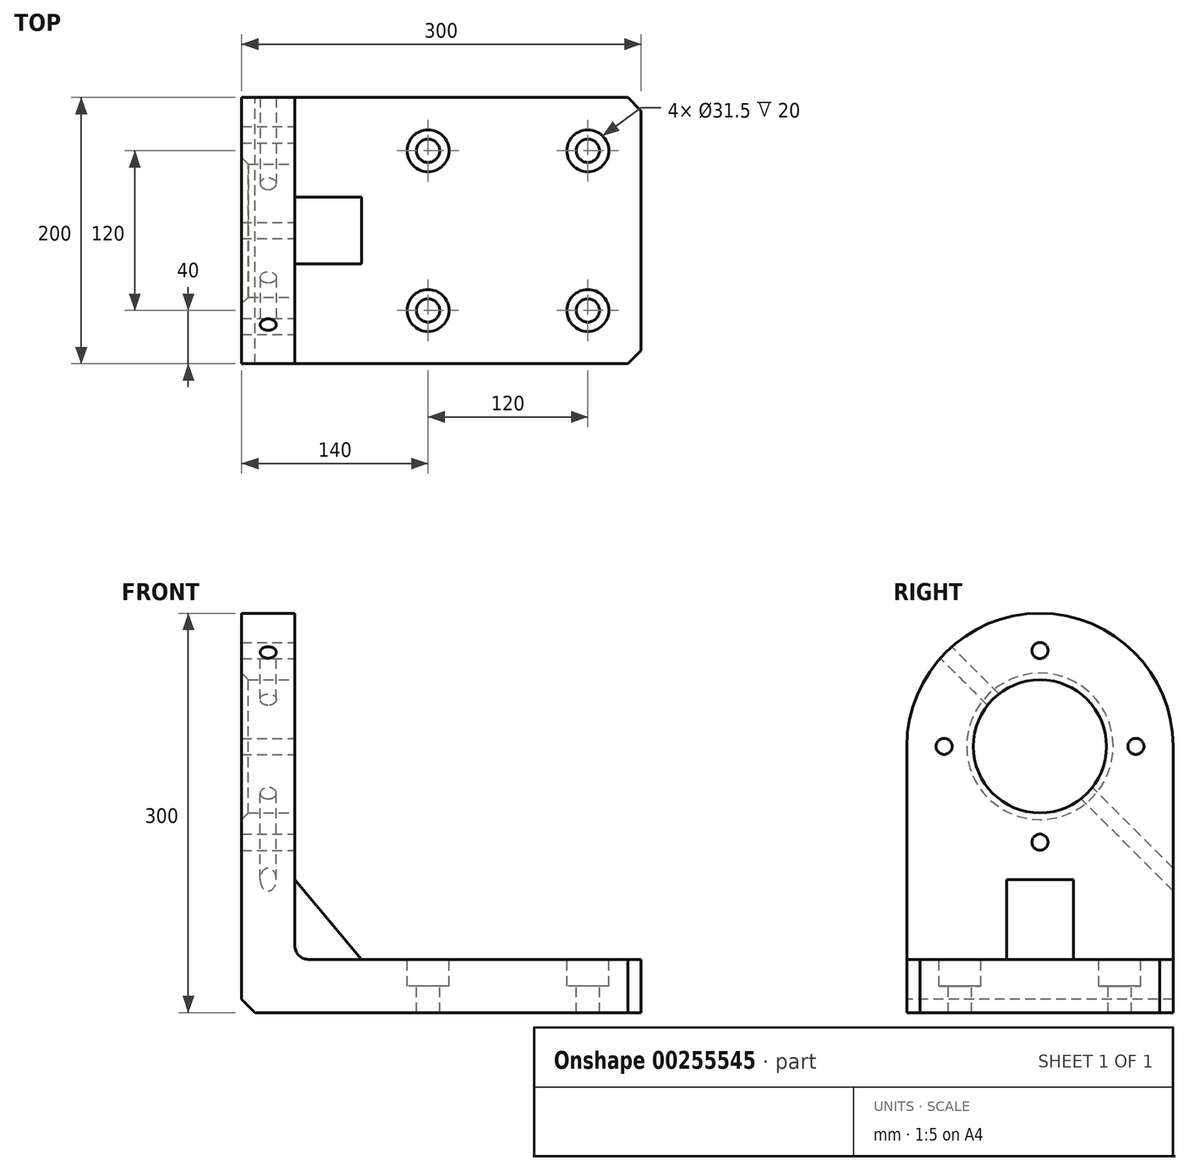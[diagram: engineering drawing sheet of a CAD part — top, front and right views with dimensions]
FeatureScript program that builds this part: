
annotation { "Feature Type Name" : "Feature", "Feature Type Description" : "" }
export const myFeature = defineFeature(function(context is Context, id is Id, definition is map)
    precondition{}
    {
        {
            var Q0;
            Q0=qCreatedBy(makeId("Front.planeOp"),FACE);
            var sketch = newSketch(context, id + "F0", { "sketchPlane" : qUnion([Q0])});
            skLineSegment(sketch, "E0", {"start": v(0, 0) * mm, "end": v(-300, 0) * mm});
            skLineSegment(sketch, "E1", {"start": v(-300, 0) * mm, "end": v(-300, 300) * mm});
            skLineSegment(sketch, "E2", {"start": v(0, 0) * mm, "end": v(0, 40) * mm});
            skLineSegment(sketch, "E3", {"start": v(-300, 300) * mm, "end": v(-260, 300) * mm});
            skLineSegment(sketch, "E4", {"start": v(0, 40) * mm, "end": v(-260, 40) * mm});
            skLineSegment(sketch, "E5", {"start": v(-260, 300) * mm, "end": v(-260, 40) * mm});
            skSolve(sketch);
        }
        {
            var Q0;
            Q0 = qSketchRegion(id + "F0", true);
            extrude(context, id + "F1", {"entities" : qUnion([Q0]), "oppositeDirection" : true, "depth" : 200 * mm});
        }
        {
            var Q0;
            Q0=makeQuery(id+"F1.opExtrude","SWEPT_FACE",FACE,{"disambiguationData":[OSD([sQuery(id+"F0.wireOp",EDGE,"E4")])]});
            var sketch = newSketch(context, id + "F2", { "sketchPlane" : qUnion([Q0])});
            skLineSegment(sketch, "E6", {"start": v(0, 160) * mm, "end": v(-40, 160) * mm, "construction": true});
            skLineSegment(sketch, "E7", {"start": v(0, 40) * mm, "end": v(-40, 40) * mm, "construction": true});
            skLineSegment(sketch, "E8", {"start": v(-40, 160) * mm, "end": v(-40, 40) * mm});
            skCircle(sketch, "E9", {"center": v(-40, 160) * mm, "radius": 15.75 * mm});
            skCircle(sketch, "E10", {"center": v(-40, 40) * mm, "radius": 15.75 * mm});
            skCircle(sketch, "E11", {"center": v(-160, 160) * mm, "radius": 15.75 * mm});
            skCircle(sketch, "E12", {"center": v(-160, 40) * mm, "radius": 15.75 * mm});
            skCircle(sketch, "E13", {"center": v(-160, 160) * mm, "radius": 8.75 * mm});
            skCircle(sketch, "E14", {"center": v(-160, 40) * mm, "radius": 8.75 * mm});
            skCircle(sketch, "E15", {"center": v(-40, 40) * mm, "radius": 8.75 * mm});
            skCircle(sketch, "E16", {"center": v(-40, 160) * mm, "radius": 8.75 * mm});
            skSolve(sketch);
        }
        {
            var Q0;
            Q0=makeQuery(id+"F2.imprint","IMPRINT",FACE,{"disambiguationData":[TD([[makeQuery(id+"F2.imprint","IMPRINT",EDGE,{"derivedFrom":sQuery(id+"F2.wireOp",EDGE,"E11")}),1.0]])]});
            var Q1;
            Q1=makeQuery(id+"F2.imprint","IMPRINT",FACE,{"disambiguationData":[TD([[makeQuery(id+"F2.imprint","IMPRINT",EDGE,{"derivedFrom":sQuery(id+"F2.wireOp",EDGE,"E12")}),1.0]])]});
            var Q2;
            Q2=makeQuery(id+"F2.imprint","IMPRINT",FACE,{"disambiguationData":[TD([[makeQuery(id+"F2.imprint","IMPRINT",EDGE,{"derivedFrom":sQuery(id+"F2.wireOp",EDGE,"E10")}),1.0]])]});
            var Q3;
            Q3=makeQuery(id+"F2.imprint","IMPRINT",FACE,{"disambiguationData":[TD([[makeQuery(id+"F2.imprint","IMPRINT",EDGE,{"derivedFrom":sQuery(id+"F2.wireOp",EDGE,"E9")}),1.0]])]});
            extrude(context, id + "F3", {"entities" : qUnion([Q0, Q1, Q2, Q3]), "operationType" : NewBodyOperationType.REMOVE, "oppositeDirection" : true, "depth" : 20 * mm});
        }
        {
            var Q0;
            Q0=makeQuery(id+"F3.boolean.opBoolean","SPLIT",FACE,{"disambiguationData":[TD([makeQuery(id+"F3.opExtrude","SWEPT_FACE",FACE,{"disambiguationData":[OSD([sQuery(id+"F2.wireOp",EDGE,"E13")])]})])],"derivedFrom":makeQuery(id+"F1.opExtrude","SWEPT_FACE",FACE,{"disambiguationData":[OSD([sQuery(id+"F0.wireOp",EDGE,"E4")])]})});
            var Q1;
            Q1=makeQuery(id+"F3.boolean.opBoolean","SPLIT",FACE,{"disambiguationData":[TD([makeQuery(id+"F3.opExtrude","SWEPT_FACE",FACE,{"disambiguationData":[OSD([sQuery(id+"F2.wireOp",EDGE,"E16")])]})])],"derivedFrom":makeQuery(id+"F1.opExtrude","SWEPT_FACE",FACE,{"disambiguationData":[OSD([sQuery(id+"F0.wireOp",EDGE,"E4")])]})});
            var Q2;
            Q2=makeQuery(id+"F3.boolean.opBoolean","SPLIT",FACE,{"disambiguationData":[TD([makeQuery(id+"F3.opExtrude","SWEPT_FACE",FACE,{"disambiguationData":[OSD([sQuery(id+"F2.wireOp",EDGE,"E15")])]})])],"derivedFrom":makeQuery(id+"F1.opExtrude","SWEPT_FACE",FACE,{"disambiguationData":[OSD([sQuery(id+"F0.wireOp",EDGE,"E4")])]})});
            var Q3;
            Q3=makeQuery(id+"F3.boolean.opBoolean","SPLIT",FACE,{"disambiguationData":[TD([makeQuery(id+"F3.opExtrude","SWEPT_FACE",FACE,{"disambiguationData":[OSD([sQuery(id+"F2.wireOp",EDGE,"E14")])]})])],"derivedFrom":makeQuery(id+"F1.opExtrude","SWEPT_FACE",FACE,{"disambiguationData":[OSD([sQuery(id+"F0.wireOp",EDGE,"E4")])]})});
            extrude(context, id + "F4", {"entities" : qUnion([Q0, Q1, Q2, Q3]), "operationType" : NewBodyOperationType.REMOVE, "endBound" : BoundingType.THROUGH_ALL, "oppositeDirection" : true, "depth" : 25 * mm});
        }
        {
            var Q0;
            Q0=makeQuery(id+"F1.opExtrude","SWEPT_FACE",FACE,{"disambiguationData":[OSD([sQuery(id+"F0.wireOp",EDGE,"E5")])]});
            var sketch = newSketch(context, id + "F5", { "sketchPlane" : qUnion([Q0])});
            skArc(sketch, "E17", {"start": v(200, 200) * mm, "mid": v(100, 300) * mm, "end": v(0, 200) * mm});
            skPoint(sketch, "E18.start.orphan", {"position": v(100, 300) * mm});
            skPoint(sketch, "E19.orphan", {"position": v(200, 200) * mm});
            skCircle(sketch, "E20", {"center": v(100, 200) * mm, "radius": 72 * mm});
            skCircle(sketch, "E21", {"center": v(100, 200) * mm, "radius": 50 * mm});
            skCircle(sketch, "E22", {"center": v(100, 272) * mm, "radius": 5.8 * mm});
            skCircle(sketch, "E23", {"center": v(100, 128) * mm, "radius": 5.8 * mm});
            skCircle(sketch, "E24", {"center": v(172, 200) * mm, "radius": 5.8 * mm});
            skCircle(sketch, "E25", {"center": v(28, 200) * mm, "radius": 5.8 * mm});
            skSolve(sketch);
        }
        {
            var Q0;
            {var subQ0=sQuery(id+"F5.wireOp",EDGE,"E17");var subQ1=sQuery(id+"F0.wireOp",EDGE,"E5");var subQ2=makeQuery(id+"F1.opExtrude","CAP_EDGE",EDGE,{"disambiguationData":[OSD([subQ1])],"isStart":true});var subQ3=makeQuery(id+"F5.imprint","INTERSECT",VERTEX,{"derivedFrom":[subQ2,subQ0]});Q0=makeQuery(id+"F5.imprint","IMPRINT",FACE,{"disambiguationData":[TD([[makeQuery(id+"F5.imprint","IMPRINT",EDGE,{"disambiguationData":[TD([[subQ3,1.0]])],"derivedFrom":subQ0}),-1.0]])]});}
            var Q1;
            {var subQ0=sQuery(id+"F5.wireOp",EDGE,"E17");var subQ1=sQuery(id+"F0.wireOp",EDGE,"E5");var subQ2=makeQuery(id+"F1.opExtrude","CAP_EDGE",EDGE,{"disambiguationData":[OSD([subQ1])],"isStart":false});var subQ3=makeQuery(id+"F5.imprint","INTERSECT",VERTEX,{"derivedFrom":[subQ2,subQ0]});Q1=makeQuery(id+"F5.imprint","IMPRINT",FACE,{"disambiguationData":[TD([[makeQuery(id+"F5.imprint","IMPRINT",EDGE,{"disambiguationData":[TD([[subQ3,-1.0]])],"derivedFrom":subQ0}),-1.0]])]});}
            extrude(context, id + "F6", {"entities" : qUnion([Q0, Q1]), "operationType" : NewBodyOperationType.REMOVE, "oppositeDirection" : true, "depth" : 89 * mm});
        }
        {
            var Q0;
            Q0=makeQuery(id+"F5.imprint","IMPRINT",FACE,{"disambiguationData":[TD([[makeQuery(id+"F5.imprint","IMPRINT",EDGE,{"derivedFrom":sQuery(id+"F5.wireOp",EDGE,"E21")}),1.0]])]});
            extrude(context, id + "F7", {"entities" : qUnion([Q0]), "operationType" : NewBodyOperationType.REMOVE, "oppositeDirection" : true, "depth" : 221 * mm});
        }
        {
            var Q0;
            Q0=sQuery(id+"F5.wireOp",VERTEX,"E25.center");
            var Q1;
            Q1=sQuery(id+"F5.wireOp",VERTEX,"E22.center");
            var Q2;
            Q2=sQuery(id+"F5.wireOp",VERTEX,"E24.center");
            var Q3;
            Q3=sQuery(id+"F5.wireOp",VERTEX,"E23.center");
            var Q4;
            Q4=makeQuery(id+"F1.opExtrude","SWEPT_BODY",BODY,{"disambiguationData":[OSD([sQuery(id+"F0.wireOp",EDGE,"E0"),sQuery(id+"F0.wireOp",EDGE,"E1"),sQuery(id+"F0.wireOp",EDGE,"E2"),sQuery(id+"F0.wireOp",EDGE,"E3"),sQuery(id+"F0.wireOp",EDGE,"E4"),sQuery(id+"F0.wireOp",EDGE,"E5")])]});
            hole(context, id + "F8", {"style" : HoleStyle.SIMPLE, "endStyle" : HoleEndStyle.THROUGH, "standardTappedOrClearance" : lookupTablePath({ "standard" : "ISO", "engagement" : "75%", "pitch" : "2 mm", "size" : "M14", "type" : "Tapped" }), "standardBlindInLast" : lookupTablePath({ "standard" : "ISO", "engagement" : "75%", "pitch" : "2 mm", "size" : "M14", "type" : "Tapped" }), "holeDiameter" : 12.1 * mm, "showTappedDepth" : true, "tappedDepth" : 12 * mm, "tapClearance" : 3, "locations" : qUnion([Q0, Q1, Q2, Q3]), "scope" : qUnion([Q4]), "majorDiameter" : 14 * mm});
        }
        {
            var Q0;
            Q0=makeQuery(id+"F1.opExtrude","SWEPT_FACE",FACE,{"disambiguationData":[OSD([sQuery(id+"F0.wireOp",EDGE,"E5")])]});
            var sketch = newSketch(context, id + "F9", { "sketchPlane" : qUnion([Q0])});
            skLineSegment(sketch, "E26", {"start": v(200, 40) * mm, "end": v(125, 40) * mm});
            skLineSegment(sketch, "E27.bottom", {"start": v(125, 40) * mm, "end": v(75, 40) * mm});
            skLineSegment(sketch, "E27.top", {"start": v(125, 100) * mm, "end": v(75, 100) * mm});
            skLineSegment(sketch, "E27.left", {"start": v(125, 40) * mm, "end": v(125, 100) * mm});
            skLineSegment(sketch, "E27.right", {"start": v(75, 40) * mm, "end": v(75, 100) * mm});
            skSolve(sketch);
        }
        {
            var Q0;
            Q0=makeQuery(id+"F9.imprint","IMPRINT",FACE,{"disambiguationData":[TD([[makeQuery(id+"F9.imprint","IMPRINT",EDGE,{"derivedFrom":sQuery(id+"F9.wireOp",EDGE,"E27.bottom")}),-1.0]])]});
            extrude(context, id + "F10", {"entities" : qUnion([Q0]), "operationType" : NewBodyOperationType.ADD, "depth" : 50 * mm});
        }
        {
            var Q0;
            Q0=makeQuery(id+"F10.opExtrude","SWEPT_FACE",FACE,{"disambiguationData":[OSD([sQuery(id+"F9.wireOp",EDGE,"E27.right")])]});
            var sketch = newSketch(context, id + "F11", { "sketchPlane" : qUnion([Q0])});
            skLineSegment(sketch, "E28", {"start": v(-260, 100) * mm, "end": v(-210, 40) * mm});
            skSolve(sketch);
        }
        {
            var Q0;
            Q0=makeQuery(id+"F11.imprint","IMPRINT",FACE,{"disambiguationData":[TD([[makeQuery(id+"F11.imprint","IMPRINT",EDGE,{"derivedFrom":sQuery(id+"F11.wireOp",EDGE,"E28")}),1.0]])]});
            extrude(context, id + "F12", {"entities" : qUnion([Q0]), "operationType" : NewBodyOperationType.REMOVE, "endBound" : BoundingType.THROUGH_ALL, "oppositeDirection" : true, "depth" : 157.8 * mm});
        }
        {
            var Q0;
            {var subQ0=sQuery(id+"F0.wireOp",EDGE,"E5");var subQ1=sQuery(id+"F0.wireOp",EDGE,"E4");Q0=makeQuery(id+"F10.boolean.opBoolean","SPLIT",EDGE,{"disambiguationData":[TD([makeQuery(id+"F10.opExtrude","SWEPT_FACE",FACE,{"disambiguationData":[OSD([sQuery(id+"F9.wireOp",EDGE,"E27.right")])]})])],"derivedFrom":makeQuery(id+"F1.opExtrude","SWEPT_EDGE",EDGE,{"disambiguationData":[OSD([subQ1,subQ0])]})});}
            var Q1;
            {var subQ0=sQuery(id+"F0.wireOp",EDGE,"E5");var subQ1=sQuery(id+"F0.wireOp",EDGE,"E4");Q1=makeQuery(id+"F10.boolean.opBoolean","SPLIT",EDGE,{"disambiguationData":[TD([makeQuery(id+"F10.opExtrude","SWEPT_FACE",FACE,{"disambiguationData":[OSD([sQuery(id+"F9.wireOp",EDGE,"E27.left")])]})])],"derivedFrom":makeQuery(id+"F1.opExtrude","SWEPT_EDGE",EDGE,{"disambiguationData":[OSD([subQ1,subQ0])]})});}
            fillet(context, id + "F13", {"entities" : qUnion([Q0, Q1]), "radius" : 10 * mm, "tangentPropagation" : true, "allowEdgeOverflow" : false});
        }
        {
            var Q0;
            Q0=makeQuery(id+"F1.opExtrude","CAP_EDGE",EDGE,{"disambiguationData":[OSD([sQuery(id+"F0.wireOp",EDGE,"E2")])],"isStart":true});
            var Q1;
            Q1=makeQuery(id+"F1.opExtrude","CAP_EDGE",EDGE,{"disambiguationData":[OSD([sQuery(id+"F0.wireOp",EDGE,"E2")])],"isStart":false});
            chamfer(context, id + "F14", {"entities" : qUnion([Q0, Q1]), "width" : 10 * mm, "tangentPropagation" : true});
        }
        {
            var Q0;
            Q0=makeQuery(id+"F7.boolean.opBoolean","COPY",EDGE,{"derivedFrom":makeQuery(id+"F7.opExtrude","CAP_EDGE",EDGE,{"disambiguationData":[OSD([sQuery(id+"F5.wireOp",EDGE,"E21")])],"isStart":true})});
            var Q1;
            Q1=makeQuery(id+"F7.boolean.opBoolean","INTERSECT",EDGE,{"derivedFrom":[makeQuery(id+"F1.opExtrude","SWEPT_FACE",FACE,{"disambiguationData":[OSD([sQuery(id+"F0.wireOp",EDGE,"E1")])]}),makeQuery(id+"F7.opExtrude","SWEPT_FACE",FACE,{"disambiguationData":[OSD([sQuery(id+"F5.wireOp",EDGE,"E21")])]})]});
            chamfer(context, id + "F15", {"entities" : qUnion([Q0, Q1]), "width" : 5 * mm, "tangentPropagation" : true});
        }
        {
            var Q0;
            Q0=makeQuery(id+"F1.opExtrude","SWEPT_EDGE",EDGE,{"disambiguationData":[OSD([sQuery(id+"F0.wireOp",EDGE,"E0"),sQuery(id+"F0.wireOp",EDGE,"E1")])]});
            chamfer(context, id + "F16", {"entities" : qUnion([Q0]), "width" : 10 * mm, "tangentPropagation" : true});
        }
        {
            var Q0;
            Q0=makeQuery(id+"F1.opExtrude","SWEPT_FACE",FACE,{"disambiguationData":[OSD([sQuery(id+"F0.wireOp",EDGE,"E1")])]});
            var sketch = newSketch(context, id + "F17", { "sketchPlane" : qUnion([Q0])});
            skLineSegment(sketch, "E29", {"start": v(-100, 200) * mm, "end": v(0, 200) * mm});
            skLineSegment(sketch, "E30", {"start": v(-100, 200) * mm, "end": v(-29.29, 270.71) * mm});
            skSolve(sketch);
        }
        {
            var Q0;
            Q0=sQuery(id+"F17.wireOp",VERTEX,"E30.end");
            var Q1;
            Q1=sQuery(id+"F17.wireOp",EDGE,"E30");
            cPlane(context, id + "F18", {"entities" : qUnion([Q0, Q1]), "cplaneType" : CPlaneType.LINE_POINT, "offset" : 25 * mm, "width" : 150 * mm, "height" : 150 * mm});
        }
        {
            var Q0;
            Q0=qCreatedBy(id+"F18.planeOp",FACE);
            var sketch = newSketch(context, id + "F19", { "sketchPlane" : qUnion([Q0])});
            skLineSegment(sketch, "E31", {"start": v(-300, 212.13) * mm, "end": v(-260, 212.13) * mm});
            skCircle(sketch, "E32", {"center": v(-280, 212.13) * mm, "radius": 5.8 * mm});
            skSolve(sketch);
        }
        {
            var Q0;
            Q0=sQuery(id+"F19.wireOp",VERTEX,"E32.center");
            var Q1;
            Q1=makeQuery(id+"F1.opExtrude","SWEPT_BODY",BODY,{"disambiguationData":[OSD([sQuery(id+"F0.wireOp",EDGE,"E0"),sQuery(id+"F0.wireOp",EDGE,"E1"),sQuery(id+"F0.wireOp",EDGE,"E2"),sQuery(id+"F0.wireOp",EDGE,"E3"),sQuery(id+"F0.wireOp",EDGE,"E4"),sQuery(id+"F0.wireOp",EDGE,"E5")])]});
            hole(context, id + "F20", {"style" : HoleStyle.SIMPLE, "endStyle" : HoleEndStyle.THROUGH, "standardTappedOrClearance" : lookupTablePath({ "standard" : "ISO", "engagement" : "75%", "pitch" : "2 mm", "size" : "M14", "type" : "Tapped" }), "standardBlindInLast" : lookupTablePath({ "standard" : "ISO", "engagement" : "75%", "pitch" : "2 mm", "size" : "M14", "type" : "Tapped" }), "holeDiameter" : 12.1 * mm, "showTappedDepth" : true, "tappedDepth" : 12 * mm, "tapClearance" : 3, "locations" : qUnion([Q0]), "scope" : qUnion([Q1]), "majorDiameter" : 14 * mm});
        }
    });
